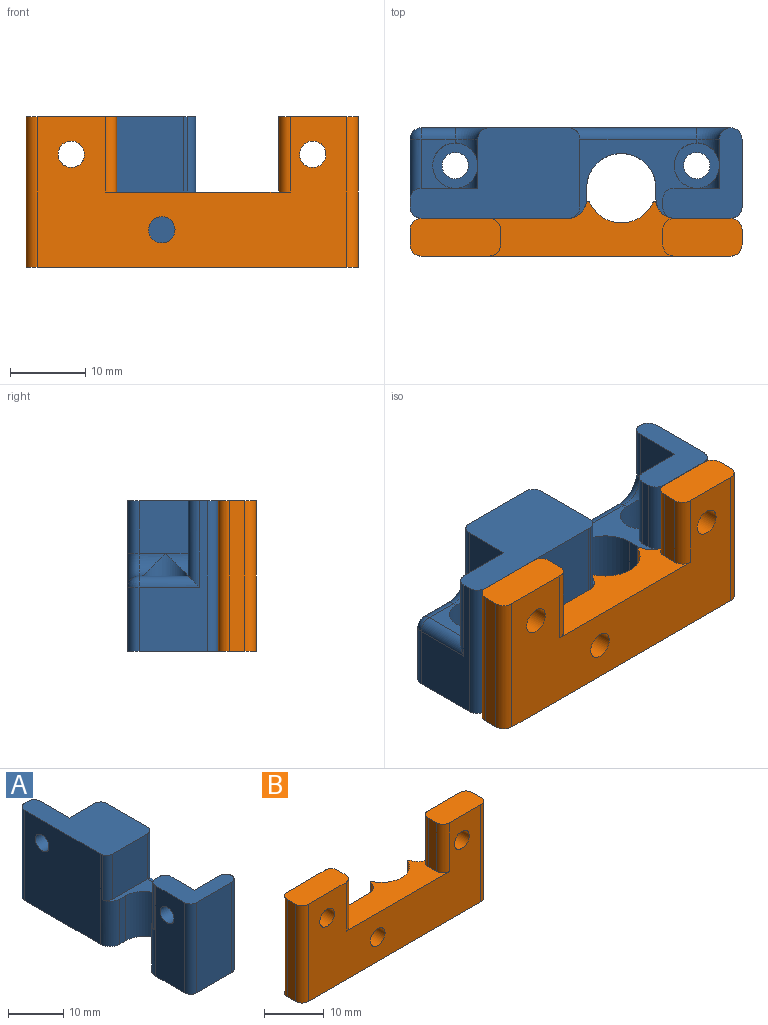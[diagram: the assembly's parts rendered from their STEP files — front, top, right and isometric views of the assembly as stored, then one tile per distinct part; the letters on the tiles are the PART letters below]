
ASSEMBLY  parts=2 mates=1
PART A: 49 faces, bbox 12x44x20 mm
  f0: plane 20x9mm, normal (0,1,0), area 88mm2, adj f1,f10,f31,f34,f39,f40
  f1: plane 22.5x12mm, normal (0,0,1), area 195.6mm2, adj f0,f9,f15,f16,f20,f23,f31,f35
  f2: cylinder r=4.6mm len=10mm, axis (0,0,-1), area 144.5mm2, adj f3,f4,f10,f21
  f3: plane 10x1.5mm, normal (0,1,0), area 15mm2, adj f2,f10,f21,f48
  f4: plane 10x1.5mm, normal (0,-1,0), area 15mm2, adj f2,f10,f21,f47
  f5: plane 12x10.5mm, normal (0,0,1), area 63.6mm2, adj f8,f17,f18,f19,f24,f32,f33,f45
  f6: cylinder r=1.75mm len=4mm, axis (0,0,-1), area 44mm2, adj f10,f12
  f7: cylinder r=1.75mm len=4mm, axis (0,0,-1), area 44mm2, adj f10,f14
  f8: plane 20x9mm, normal (0,-1,0), area 180mm2, adj f5,f10,f32,f33
  f9: plane 41x20mm, normal (1,0,0), area 477.9mm2, adj f1,f10,f33,f34,f35,f36,f37,f41
  f10: plane 44x12mm, normal (0,0,-1), area 434.1mm2, adj f0,f2,f3,f4,f6,f7,f8,f9
  f11: cylinder r=3mm len=9mm, axis (0,0,1), area 123.4mm2, adj f12,f21,f29,f30
  f12: plane 6x6mm, normal (0,0,1), area 18.7mm2, adj f6,f11
  f13: cylinder r=3mm len=9mm, axis (0,0,1), area 123.4mm2, adj f14,f22,f27,f28
  f14: plane 6x6mm, normal (0,0,1), area 18.7mm2, adj f7,f13
  f15: plane 10x7.5mm, normal (1,0,0), area 63.4mm2, adj f1,f16,f22,f26,f28,f39
  f16: plane 7x6.5mm, normal (0,1,0), area 45.5mm2, adj f1,f15,f27,f28,f35
  f17: plane 10x1mm, normal (0,1,0), area 10mm2, adj f5,f21,f45,f46
  f18: plane 10x6mm, normal (1,0,0), area 48.4mm2, adj f5,f19,f21,f25,f30,f46
  f19: plane 7x6.5mm, normal (0,1,0), area 45.5mm2, adj f5,f18,f29,f30,f33
  f20: plane 10x9mm, normal (0,-1,0), area 90mm2, adj f1,f21,f42,f44
  f21: plane 16.66x10.46mm, normal (0,0,1), area 59.3mm2, adj f2,f3,f4,f11,f17,f18,f20,f29
  f22: plane 6.5x4.5mm, normal (0,0,1), area 15.1mm2, adj f13,f15,f27,f37,f40
  f23: plane 20x19.4mm, normal (-1,0,0), area 378.4mm2, adj f1,f10,f26,f31,f47
  f24: plane 20x7.4mm, normal (-1,0,0), area 138.4mm2, adj f5,f10,f25,f32,f48
  f25: cylinder r=1.75mm len=4mm, axis (1,0,0), area 44mm2, adj f18,f24
  f26: cylinder r=1.75mm len=4mm, axis (1,0,0), area 44mm2, adj f15,f23
  f27: cylinder r=3mm len=3.5mm, axis (-1,0,0), area 7.5mm2, adj f13,f16,f22,f36
  f28: cylinder r=3mm len=3mm, axis (1,0,0), area 5.1mm2, adj f13,f15,f16
  f29: cylinder r=3mm len=3.5mm, axis (1,0,0), area 7.5mm2, adj f11,f19,f21,f41
  f30: cylinder r=3mm len=3mm, axis (1,0,0), area 5.1mm2, adj f11,f18,f19
  f31: cylinder r=1.5mm len=20mm, axis (0,0,1), area 47.1mm2, adj f0,f1,f10,f23
  f32: cylinder r=1.5mm len=20mm, axis (0,0,-1), area 47.1mm2, adj f5,f8,f10,f24
  f33: cylinder r=1.5mm len=20mm, axis (0,0,1), area 63.6mm2, adj f5,f8,f9,f10,f19,f41
  f34: cylinder r=1.5mm len=8.5mm, axis (0,0,-1), area 20mm2, adj f0,f9,f10,f38
  f35: cylinder r=1.5mm len=7mm, axis (0,0,1), area 16.5mm2, adj f1,f9,f16,f36
  f36: torus R=4.5mm, axis (-1,0,0), area 13.1mm2, adj f9,f27,f35,f37
  f37: cylinder r=1.5mm len=4.5mm, axis (0,-1,0), area 10.6mm2, adj f9,f22,f36,f38
  f38: sphere r=1.5mm, area 3.5mm2, adj f34,f37,f40
  f39: cylinder r=1.5mm len=11.5mm, axis (0,0,1), area 24.8mm2, adj f0,f1,f15,f40
  f40: cylinder r=1.5mm len=8mm, axis (1,0,0), area 16.6mm2, adj f0,f22,f38,f39
  f41: torus R=4.5mm, axis (-1,0,0), area 13.1mm2, adj f9,f29,f33,f43
  f42: cylinder r=1.5mm len=11.5mm, axis (0,0,-1), area 24.8mm2, adj f1,f9,f20,f43
  f43: cylinder r=1.5mm len=17mm, axis (0,-1,0), area 37.8mm2, adj f9,f21,f41,f42
  f44: cylinder r=1.5mm len=10mm, axis (0,0,1), area 20.1mm2, adj f1,f20,f21,f47
  f45: cylinder r=1.5mm len=10mm, axis (0,0,1), area 20.1mm2, adj f5,f17,f21,f48
  f46: cylinder r=1.5mm len=10mm, axis (0,0,1), area 23.6mm2, adj f5,f17,f18,f21
  f47: cylinder r=2.5mm len=20mm, axis (0,0,-1), area 43.7mm2, adj f1,f4,f10,f21,f23,f44
  f48: cylinder r=2.5mm len=20mm, axis (0,0,1), area 43.7mm2, adj f3,f5,f10,f21,f24,f45
PART B: 27 faces, bbox 44x7.2x20 mm
  f0: plane 10.5x5mm, normal (0,0,1), area 50.6mm2, adj f6,f7,f8,f12,f19,f20,f25,f26
  f1: cylinder r=2.5mm len=10mm, axis (0,0,-1), area 34.4mm2, adj f2,f8,f9,f15
  f2: plane 24.6x7.22mm, normal (0,0,1), area 115.2mm2, adj f1,f3,f4,f6,f8,f10,f12,f13
  f3: cylinder r=4.6mm len=10mm, axis (0,0,-1), area 104.7mm2, adj f2,f9,f14,f15
  f4: plane 20x19.4mm, normal (0,1,0), area 264.8mm2, adj f2,f9,f11,f13,f17,f18,f21,f23
  f5: plane 20x2mm, normal (-1,0,0), area 40mm2, adj f9,f11,f23,f24
  f6: plane 41x20mm, normal (0,-1,0), area 546.1mm2, adj f0,f2,f9,f11,f16,f17,f18,f20
  f7: plane 20x2mm, normal (1,0,0), area 40mm2, adj f0,f9,f25,f26
  f8: plane 20x7.5mm, normal (0,1,0), area 139.4mm2, adj f0,f1,f2,f9,f16,f19,f26
  f9: plane 44x7.22mm, normal (0,0,-1), area 223.9mm2, adj f1,f3,f4,f5,f6,f7,f8,f13
  f10: plane 10x2mm, normal (1,0,0), area 20mm2, adj f2,f11,f21,f22
  f11: plane 12x5mm, normal (0,0,1), area 58.1mm2, adj f4,f5,f6,f10,f21,f22,f23,f24
  f12: plane 10x2mm, normal (-1,0,0), area 20mm2, adj f0,f2,f19,f20
  f13: cylinder r=2.5mm len=10mm, axis (0,0,1), area 34.4mm2, adj f2,f4,f9,f14
  f14: cylinder r=0.25mm len=10mm, axis (0,0,-1), area 6.3mm2, adj f2,f3,f9,f13
  f15: cylinder r=0.25mm len=10mm, axis (0,0,-1), area 6.3mm2, adj f1,f2,f3,f9
  f16: cylinder r=1.75mm len=5mm, axis (0,-1,0), area 55mm2, adj f6,f8
  f17: cylinder r=1.75mm len=5mm, axis (0,-1,0), area 55mm2, adj f4,f6
  f18: cylinder r=1.75mm len=5mm, axis (0,-1,0), area 55mm2, adj f4,f6
  f19: cylinder r=1.5mm len=10mm, axis (0,0,-1), area 23.6mm2, adj f0,f2,f8,f12
  f20: cylinder r=1.5mm len=10mm, axis (0,0,1), area 23.6mm2, adj f0,f2,f6,f12
  f21: cylinder r=1.5mm len=10mm, axis (0,0,-1), area 23.6mm2, adj f2,f4,f10,f11
  f22: cylinder r=1.5mm len=10mm, axis (0,0,-1), area 23.6mm2, adj f2,f6,f10,f11
  f23: cylinder r=1.5mm len=20mm, axis (0,0,1), area 47.1mm2, adj f4,f5,f9,f11
  f24: cylinder r=1.5mm len=20mm, axis (0,0,1), area 47.1mm2, adj f5,f6,f9,f11
  f25: cylinder r=1.5mm len=20mm, axis (0,0,-1), area 47.1mm2, adj f0,f6,f7,f9
  f26: cylinder r=1.5mm len=20mm, axis (0,0,-1), area 47.1mm2, adj f0,f7,f8,f9
PLACE A rot(axis=(0,0,1),90deg) t=(11.78,19.41,-3.68)mm
PLACE B t=(-10.22,7.41,-3.68)mm
MATE fastened A.f26 <-> B.f17  axis (0,-1,0) through (-4.22,12.41,11.32)mm
